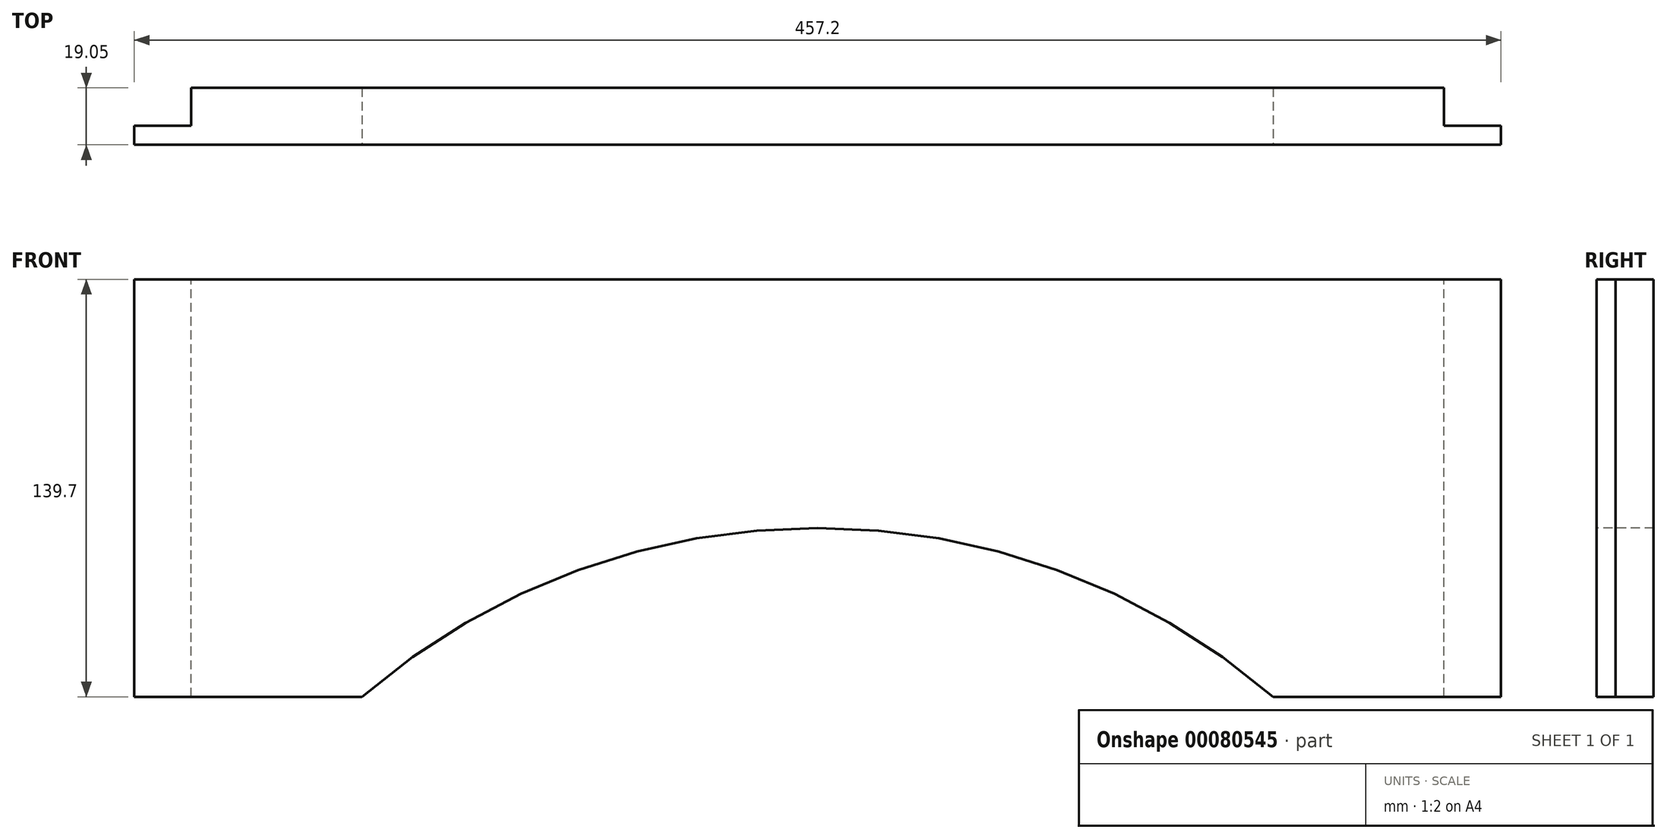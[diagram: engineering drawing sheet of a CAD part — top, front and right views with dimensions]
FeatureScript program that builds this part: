
annotation { "Feature Type Name" : "Feature", "Feature Type Description" : "" }
export const myFeature = defineFeature(function(context is Context, id is Id, definition is map)
    precondition{}
    {
        {
            var Q0;
            Q0=qCreatedBy(makeId("Front.planeOp"),FACE);
            var sketch = newSketch(context, id + "F0", { "sketchPlane" : qUnion([Q0])});
            skLineSegment(sketch, "E0.bottom", {"start": v(0, 0) * mm, "end": v(-457.2, 0) * mm});
            skLineSegment(sketch, "E0.top", {"start": v(0, 139.7) * mm, "end": v(-457.2, 139.7) * mm});
            skLineSegment(sketch, "E0.left", {"start": v(0, 0) * mm, "end": v(0, 139.7) * mm});
            skLineSegment(sketch, "E0.right", {"start": v(-457.2, 0) * mm, "end": v(-457.2, 139.7) * mm});
            skSolve(sketch);
        }
        {
            var Q0;
            Q0=makeQuery(id+"F0.imprint","IMPRINT",FACE,{"disambiguationData":[TD([[makeQuery(id+"F0.imprint","IMPRINT",EDGE,{"derivedFrom":sQuery(id+"F0.wireOp",EDGE,"E0.bottom")}),-1.0]])]});
            extrude(context, id + "F1", {"entities" : qUnion([Q0]), "depth" : 19.05 * mm});
        }
        {
            var Q0;
            Q0=makeQuery(id+"F1.opExtrude","SWEPT_FACE",FACE,{"disambiguationData":[OSD([sQuery(id+"F0.wireOp",EDGE,"E0.top")])]});
            var sketch = newSketch(context, id + "F2", { "sketchPlane" : qUnion([Q0])});
            skLineSegment(sketch, "E1", {"start": v(-19.05, 0) * mm, "end": v(-19.05, -12.7) * mm});
            skLineSegment(sketch, "E2", {"start": v(-19.05, -12.7) * mm, "end": v(0, -12.7) * mm});
            skSolve(sketch);
        }
        {
            var Q0;
            {var subQ0=sQuery(id+"F2.wireOp",EDGE,"E1");Q0=makeQuery(id+"F2.imprint","IMPRINT",FACE,{"disambiguationData":[TD([[makeQuery(id+"F2.imprint","IMPRINT",EDGE,{"derivedFrom":subQ0}),1.0]])]});}
            extrude(context, id + "F3", {"entities" : qUnion([Q0]), "operationType" : NewBodyOperationType.REMOVE, "endBound" : BoundingType.THROUGH_ALL, "oppositeDirection" : true, "depth" : 25.4 * mm});
        }
        {
            var Q0;
            Q0=makeQuery(id+"F1.opExtrude","SWEPT_FACE",FACE,{"disambiguationData":[OSD([sQuery(id+"F0.wireOp",EDGE,"E0.top")])]});
            var sketch = newSketch(context, id + "F4", { "sketchPlane" : qUnion([Q0])});
            skLineSegment(sketch, "E3", {"start": v(-457.2, -12.7) * mm, "end": v(-438.15, -12.7) * mm});
            skLineSegment(sketch, "E4", {"start": v(-438.15, -12.7) * mm, "end": v(-438.15, 0) * mm});
            skSolve(sketch);
        }
        {
            var Q0;
            {var subQ0=sQuery(id+"F4.wireOp",EDGE,"E3");Q0=makeQuery(id+"F4.imprint","IMPRINT",FACE,{"disambiguationData":[TD([[makeQuery(id+"F4.imprint","IMPRINT",EDGE,{"derivedFrom":subQ0}),1.0]])]});}
            extrude(context, id + "F5", {"entities" : qUnion([Q0]), "operationType" : NewBodyOperationType.REMOVE, "endBound" : BoundingType.THROUGH_ALL, "oppositeDirection" : true, "depth" : 25.4 * mm});
        }
        {
            var Q0;
            Q0=makeQuery(id+"F1.opExtrude","CAP_FACE",FACE,{"disambiguationData":[OSD([sQuery(id+"F0.wireOp",EDGE,"E0.bottom"),sQuery(id+"F0.wireOp",EDGE,"E0.top"),sQuery(id+"F0.wireOp",EDGE,"E0.left"),sQuery(id+"F0.wireOp",EDGE,"E0.right")])],"isStart":false});
            var sketch = newSketch(context, id + "F6", { "sketchPlane" : qUnion([Q0])});
            skArc(sketch, "E5", {"start": v(-76.2, 0) * mm, "mid": v(-228.6, 56.52) * mm, "end": v(-381, 0) * mm});
            skSolve(sketch);
        }
        {
            var Q0;
            {var subQ0=sQuery(id+"F6.wireOp",EDGE,"E5");Q0=makeQuery(id+"F6.imprint","IMPRINT",FACE,{"disambiguationData":[TD([[makeQuery(id+"F6.imprint","IMPRINT",EDGE,{"derivedFrom":subQ0}),1.0]])]});}
            extrude(context, id + "F7", {"entities" : qUnion([Q0]), "operationType" : NewBodyOperationType.REMOVE, "endBound" : BoundingType.THROUGH_ALL, "oppositeDirection" : true, "depth" : 25.4 * mm});
        }
    });
